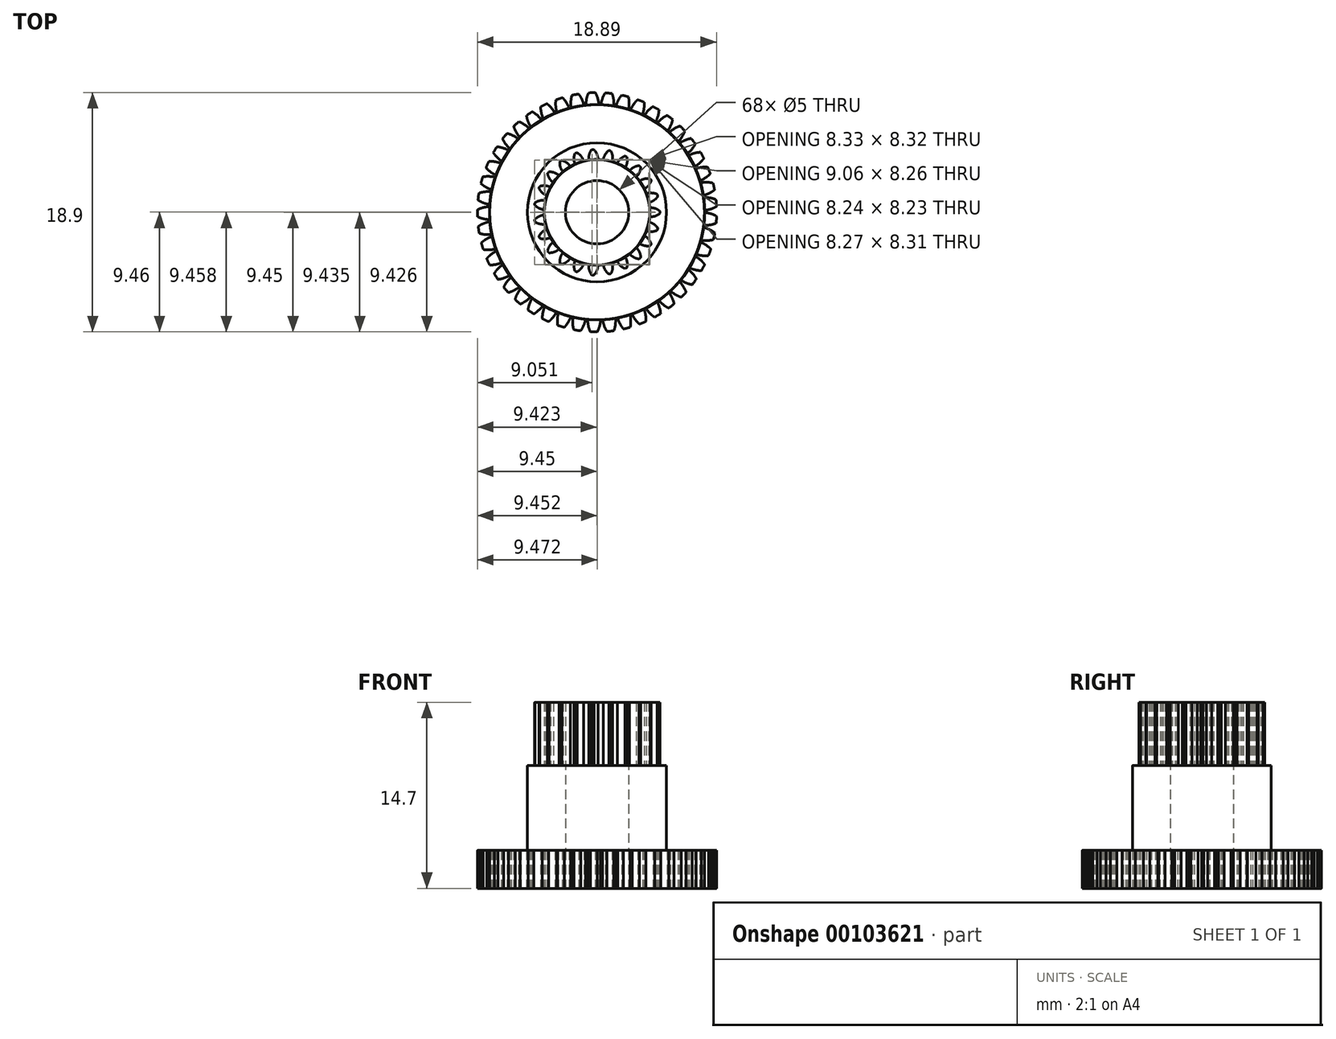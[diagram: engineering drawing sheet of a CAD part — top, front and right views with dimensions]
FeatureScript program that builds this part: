
annotation { "Feature Type Name" : "Feature", "Feature Type Description" : "" }
export const myFeature = defineFeature(function(context is Context, id is Id, definition is map)
    precondition{}
    {
        {
            var Q0;
            Q0=qCreatedBy(makeId("Top.planeOp"),FACE);
            var sketch = newSketch(context, id + "F0", { "sketchPlane" : qUnion([Q0])});
            skCircle(sketch, "E0", {"center": v(0, 0) * mm, "radius": 8.5 * mm});
            skCircle(sketch, "E1", {"center": v(0, 0) * mm, "radius": 9.17 * mm, "construction": true});
            skCircle(sketch, "E2", {"center": v(0, 0) * mm, "radius": 9.45 * mm, "construction": true});
            skLineSegment(sketch, "E3", {"start": v(0, 0) * mm, "end": v(0, 12.86) * mm, "construction": true});
            skLineSegment(sketch, "E4", {"start": v(0, 0) * mm, "end": v(-0.57, 13.35) * mm, "construction": true});
            skLineSegment(sketch, "E5", {"start": v(0, 9.17) * mm, "end": v(-6.4, 9.17) * mm, "construction": true});
            skLineSegment(sketch, "E6", {"start": v(0, 9.17) * mm, "end": v(-7.4, 6.47) * mm, "construction": true});
            skCircle(sketch, "E7", {"center": v(0, 9.17) * mm, "radius": 2.3 * mm, "construction": true});
            skCircle(sketch, "E8", {"center": v(0, 0) * mm, "radius": 8.62 * mm, "construction": true});
            skCircle(sketch, "E9", {"center": v(-2.14, 8.35) * mm, "radius": 2.3 * mm, "construction": true});
            skArc(sketch, "E10", {"start": v(0, 9.17) * mm, "mid": v(-0.06, 9.31) * mm, "end": v(-0.13, 9.45) * mm});
            skArc(sketch, "E11", {"start": v(0.15, 8.5) * mm, "mid": v(0.1, 8.84) * mm, "end": v(0, 9.17) * mm});
            skArc(sketch, "E12.MirrorCS", {"start": v(-0.87, 8.46) * mm, "mid": v(-0.85, 8.8) * mm, "end": v(-0.78, 9.14) * mm});
            skArc(sketch, "E13.MirrorCS", {"start": v(-0.78, 9.14) * mm, "mid": v(-0.74, 9.28) * mm, "end": v(-0.68, 9.43) * mm});
            skArc(sketch, "E14", {"start": v(-0.13, 9.45) * mm, "mid": v(-0.4, 9.45) * mm, "end": v(-0.68, 9.43) * mm});
            skSolve(sketch);
        }
        {
            var Q0;
            Q0 = qSketchRegion(id + "F0", true);
            extrude(context, id + "F1", {"entities" : qUnion([Q0]), "depth" : 3 * mm});
        }
        {
            var Q0;
            Q0=makeQuery(id+"F1.opExtrude","SWEPT_BODY",BODY,{"disambiguationData":[OSD([sQuery(id+"F0.wireOp",EDGE,"E0"),sQuery(id+"F0.wireOp",EDGE,"v8zbosKu-hMTk-nlC0-qCma-qfy0SiHJwD4U"),sQuery(id+"F0.wireOp",EDGE,"27a89d3e-6e36-4ed2-918c-0375e7c416ea0.MirrorCS"),sQuery(id+"F0.wireOp",EDGE,"Yo8CEICt-4u8U-YT6V-h5X9-WiJi3uYgK4uo")])]});
            var Q1;
            Q1=makeQuery(id+"F1.opExtrude","SWEPT_FACE",FACE,{"disambiguationData":[OSD([sQuery(id+"F0.wireOp",EDGE,"E0")])]});
            circularPattern(context, id + "F2", {"entities" : qUnion([Q0]), "axis" : qUnion([Q1]), "angle" : 8 * degree, "instanceCount" : 45});
        }
        {
            var Q0;
            Q0=makeQuery(id+"F1.opExtrude","CAP_FACE",FACE,{"disambiguationData":[OSD([sQuery(id+"F0.wireOp",EDGE,"E0"),sQuery(id+"F0.wireOp",EDGE,"v8zbosKu-hMTk-nlC0-qCma-qfy0SiHJwD4U"),sQuery(id+"F0.wireOp",EDGE,"27a89d3e-6e36-4ed2-918c-0375e7c416ea0.MirrorCS"),sQuery(id+"F0.wireOp",EDGE,"Yo8CEICt-4u8U-YT6V-h5X9-WiJi3uYgK4uo")])],"isStart":false});
            var sketch = newSketch(context, id + "F3", { "sketchPlane" : qUnion([Q0])});
            skCircle(sketch, "E15", {"center": v(0, 0) * mm, "radius": 5.5 * mm});
            skSolve(sketch);
        }
        {
            var Q0;
            Q0 = qSketchRegion(id + "F3", true);
            extrude(context, id + "F4", {"entities" : qUnion([Q0]), "depth" : 6.7 * mm});
        }
        {
            var Q0;
            Q0=makeQuery(id+"F4.opExtrude","CAP_FACE",FACE,{"disambiguationData":[OSD([sQuery(id+"F3.wireOp",EDGE,"E15")])],"isStart":false});
            var sketch = newSketch(context, id + "F5", { "sketchPlane" : qUnion([Q0])});
            skCircle(sketch, "E16", {"center": v(0, 0) * mm, "radius": 4.96 * mm, "construction": true});
            skCircle(sketch, "E17", {"center": v(0, 0) * mm, "radius": 4.57 * mm, "construction": true});
            skCircle(sketch, "E18", {"center": v(0, 0) * mm, "radius": 4.17 * mm});
            skLineSegment(sketch, "E19", {"start": v(0, 0) * mm, "end": v(0, 9.58) * mm, "construction": true});
            skLineSegment(sketch, "E20", {"start": v(0, 0) * mm, "end": v(-0.68, 9.96) * mm, "construction": true});
            skLineSegment(sketch, "E21", {"start": v(0, 4.57) * mm, "end": v(-5.94, 4.57) * mm, "construction": true});
            skLineSegment(sketch, "E22", {"start": v(0, 4.57) * mm, "end": v(-6.15, 2.33) * mm, "construction": true});
            skCircle(sketch, "E23", {"center": v(0, 0) * mm, "radius": 4.3 * mm, "construction": true});
            skCircle(sketch, "E24", {"center": v(0, 4.57) * mm, "radius": 1.14 * mm, "construction": true});
            skCircle(sketch, "E25", {"center": v(-1.06, 4.16) * mm, "radius": 1.14 * mm, "construction": true});
            skArc(sketch, "E26", {"start": v(0, 4.57) * mm, "mid": v(-0.1, 4.78) * mm, "end": v(-0.25, 4.96) * mm});
            skArc(sketch, "E27", {"start": v(0.08, 4.17) * mm, "mid": v(0.06, 4.37) * mm, "end": v(0, 4.57) * mm});
            skArc(sketch, "E28.MirrorCS", {"start": v(-0.62, 4.53) * mm, "mid": v(-0.55, 4.75) * mm, "end": v(-0.43, 4.95) * mm});
            skArc(sketch, "E29.MirrorCS", {"start": v(-0.64, 4.12) * mm, "mid": v(-0.65, 4.32) * mm, "end": v(-0.62, 4.53) * mm});
            skArc(sketch, "E30", {"start": v(-0.25, 4.96) * mm, "mid": v(-0.34, 4.95) * mm, "end": v(-0.43, 4.95) * mm});
            skSolve(sketch);
        }
        {
            var Q0;
            Q0 = qSketchRegion(id + "F5", true);
            extrude(context, id + "F6", {"entities" : qUnion([Q0]), "operationType" : NewBodyOperationType.ADD, "depth" : 5 * mm});
        }
        {
            var Q0;
            Q0=makeQuery(id+"F4.opExtrude","SWEPT_BODY",BODY,{"disambiguationData":[OSD([sQuery(id+"F3.wireOp",EDGE,"E15")])]});
            var Q1;
            Q1=makeQuery(id+"F6.opExtrude","SWEPT_FACE",FACE,{"disambiguationData":[OSD([sQuery(id+"F5.wireOp",EDGE,"E18")])]});
            circularPattern(context, id + "F7", {"entities" : qUnion([Q0]), "axis" : qUnion([Q1]), "angle" : 15.65 * degree, "instanceCount" : 23});
        }
        {
            var Q0;
            Q0=qCreatedBy(makeId("Top.planeOp"),FACE);
            var sketch = newSketch(context, id + "F8", { "sketchPlane" : qUnion([Q0])});
            skCircle(sketch, "E31", {"center": v(0, 0) * mm, "radius": 2.5 * mm});
            skSolve(sketch);
        }
        {
            var Q0;
            Q0 = qSketchRegion(id + "F8", true);
            extrude(context, id + "F9", {"entities" : qUnion([Q0]), "operationType" : NewBodyOperationType.REMOVE, "endBound" : BoundingType.THROUGH_ALL, "depth" : 15.55 * mm});
        }
    });
